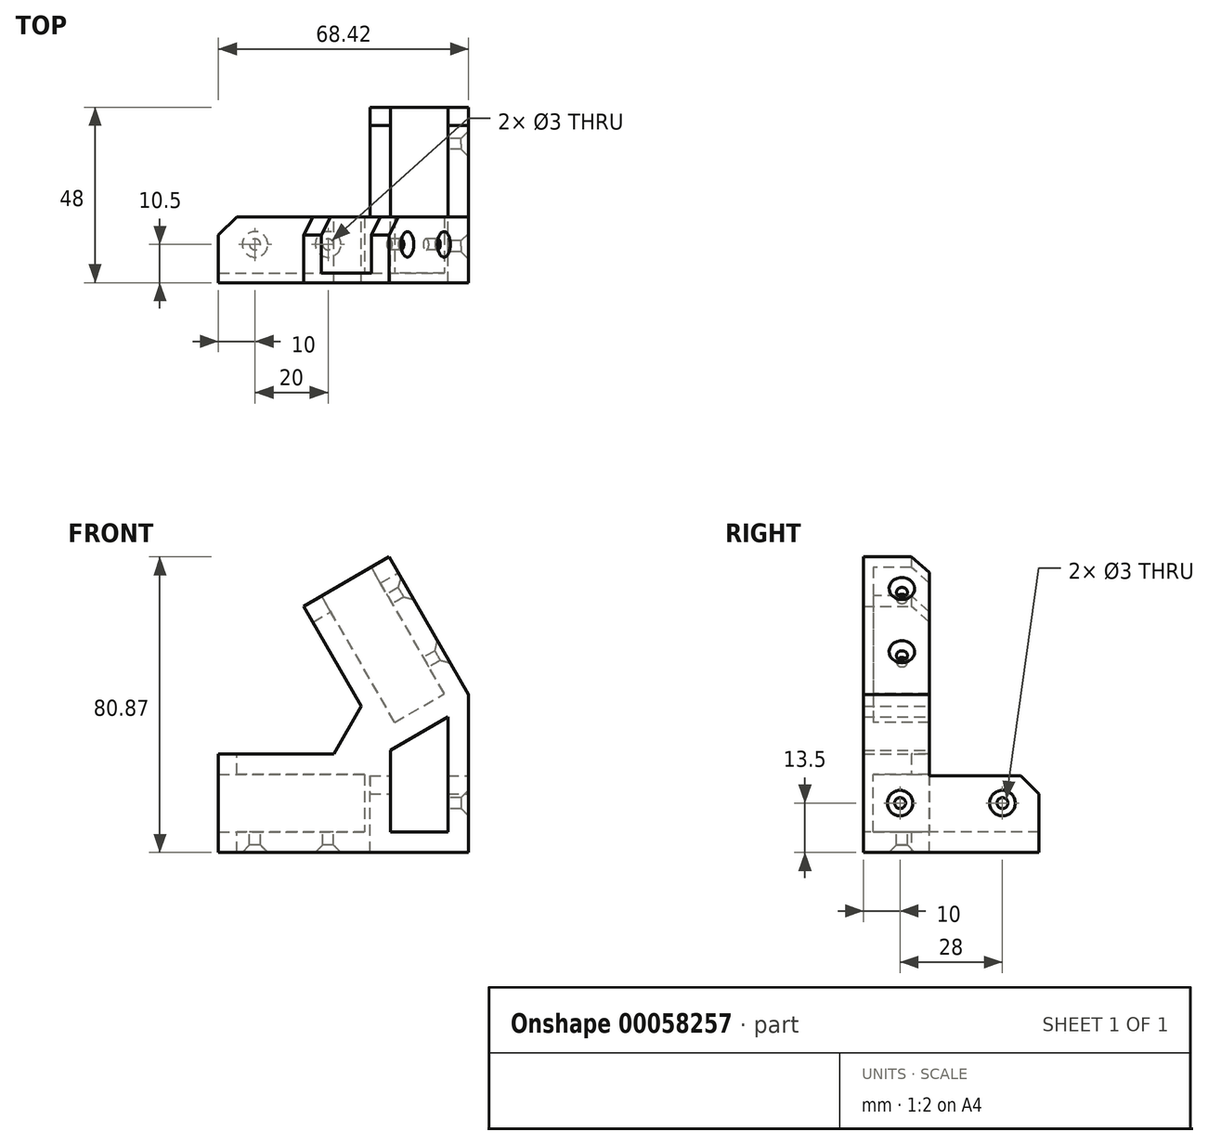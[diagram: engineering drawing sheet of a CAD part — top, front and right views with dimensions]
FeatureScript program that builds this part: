
annotation { "Feature Type Name" : "Feature", "Feature Type Description" : "" }
export const myFeature = defineFeature(function(context is Context, id is Id, definition is map)
    precondition{}
    {
        {
            var Q0;
            Q0=qCreatedBy(makeId("Front.planeOp"),FACE);
            var sketch = newSketch(context, id + "F0", { "sketchPlane" : qUnion([Q0])});
            skLineSegment(sketch, "E0", {"start": v(0, 0) * mm, "end": v(-45, 25.98) * mm, "construction": true});
            skLineSegment(sketch, "E1", {"start": v(0, 0) * mm, "end": v(-59.97, 0) * mm, "construction": true});
            skLineSegment(sketch, "E2.bottom", {"start": v(-30, 7.5) * mm, "end": v(-70, 7.5) * mm});
            skLineSegment(sketch, "E2.top", {"start": v(-30, -7.5) * mm, "end": v(-70, -7.5) * mm});
            skLineSegment(sketch, "E2.left", {"start": v(-30, 7.5) * mm, "end": v(-30, -7.5) * mm});
            skLineSegment(sketch, "E2.right", {"start": v(-70, 7.5) * mm, "end": v(-70, -7.5) * mm, "construction": true});
            skPoint(sketch, "E2.middle", {"position": v(-50, 0) * mm});
            skLineSegment(sketch, "E3", {"start": v(-70, -7.5) * mm, "end": v(-70, -13.5) * mm});
            skLineSegment(sketch, "E4", {"start": v(-70, -13.5) * mm, "end": v(-1.58, -13.5) * mm});
            skLineSegment(sketch, "E5", {"start": v(-70, 7.5) * mm, "end": v(-70, 13.5) * mm});
            skLineSegment(sketch, "E6", {"start": v(-70, 13.5) * mm, "end": v(-38.38, 13.5) * mm});
            skLineSegment(sketch, "E7.MirrorCS", {"start": v(-28.5, 64.37) * mm, "end": v(-23.3, 67.37) * mm});
            skLineSegment(sketch, "E8.MirrorCS", {"start": v(-8.5, 29.73) * mm, "end": v(-28.5, 64.37) * mm});
            skLineSegment(sketch, "E9.MirrorCS", {"start": v(-21.5, 22.23) * mm, "end": v(-8.5, 29.73) * mm});
            skLineSegment(sketch, "E10.MirrorCS", {"start": v(-21.5, 22.23) * mm, "end": v(-41.5, 56.87) * mm});
            skLineSegment(sketch, "E11.MirrorCS", {"start": v(-41.5, 56.87) * mm, "end": v(-46.7, 53.87) * mm});
            skLineSegment(sketch, "E12.MirrorCS", {"start": v(-46.7, 53.87) * mm, "end": v(-30.88, 26.5) * mm});
            skLineSegment(sketch, "E13", {"start": v(-23.3, 67.37) * mm, "end": v(-1.58, 29.73) * mm});
            skLineSegment(sketch, "E14", {"start": v(-1.58, 29.73) * mm, "end": v(-1.58, -13.5) * mm});
            skLineSegment(sketch, "E15.bottom", {"start": v(-7.58, 7.5) * mm, "end": v(-22.58, 7.5) * mm});
            skLineSegment(sketch, "E15.top", {"start": v(-7.58, -7.5) * mm, "end": v(-22.58, -7.5) * mm});
            skLineSegment(sketch, "E15.left", {"start": v(-7.58, 7.5) * mm, "end": v(-7.58, -7.5) * mm});
            skLineSegment(sketch, "E15.right", {"start": v(-22.58, 7.5) * mm, "end": v(-22.58, -7.5) * mm});
            skPoint(sketch, "E15.middle", {"position": v(-15.08, 0) * mm});
            skLineSegment(sketch, "E16", {"start": v(-30.88, 26.5) * mm, "end": v(-38.38, 13.5) * mm});
            skLineSegment(sketch, "E17", {"start": v(-30.88, 26.5) * mm, "end": v(-23.38, 13.5) * mm, "construction": true});
            skLineSegment(sketch, "E18", {"start": v(-38.38, 13.5) * mm, "end": v(-23.38, 13.5) * mm, "construction": true});
            skSolve(sketch);
        }
        {
            var Q0;
            Q0 = qSketchRegion(id + "F0", true);
            extrude(context, id + "F1", {"entities" : qUnion([Q0]), "depth" : 15 * mm});
        }
        {
            var Q0;
            Q0=makeQuery(id+"F1.opExtrude","CAP_FACE",FACE,{"disambiguationData":[OSD([sQuery(id+"F0.wireOp",EDGE,"E2.bottom"),sQuery(id+"F0.wireOp",EDGE,"E2.top"),sQuery(id+"F0.wireOp",EDGE,"E2.left"),sQuery(id+"F0.wireOp",EDGE,"E3"),sQuery(id+"F0.wireOp",EDGE,"E4"),sQuery(id+"F0.wireOp",EDGE,"E5"),sQuery(id+"F0.wireOp",EDGE,"E6"),sQuery(id+"F0.wireOp",EDGE,"E7.MirrorCS"),sQuery(id+"F0.wireOp",EDGE,"E8.MirrorCS"),sQuery(id+"F0.wireOp",EDGE,"E9.MirrorCS"),sQuery(id+"F0.wireOp",EDGE,"E10.MirrorCS"),sQuery(id+"F0.wireOp",EDGE,"E11.MirrorCS"),sQuery(id+"F0.wireOp",EDGE,"E12.MirrorCS"),sQuery(id+"F0.wireOp",EDGE,"E13"),sQuery(id+"F0.wireOp",EDGE,"E14"),sQuery(id+"F0.wireOp",EDGE,"E15.bottom"),sQuery(id+"F0.wireOp",EDGE,"E15.top"),sQuery(id+"F0.wireOp",EDGE,"E15.left"),sQuery(id+"F0.wireOp",EDGE,"E15.right")])],"isStart":false});
            var sketch = newSketch(context, id + "F2", { "sketchPlane" : qUnion([Q0])});
            skLineSegment(sketch, "E19", {"start": v(-70, 13.5) * mm, "end": v(-70, -13.5) * mm});
            skLineSegment(sketch, "E20", {"start": v(-46.7, 53.87) * mm, "end": v(-23.3, 67.37) * mm});
            skLineSegment(sketch, "E21.0", {"start": v(-23.3, 67.37) * mm, "end": v(-1.58, 29.73) * mm});
            skLineSegment(sketch, "E21.1", {"start": v(-1.58, 29.73) * mm, "end": v(-1.58, -13.5) * mm});
            skLineSegment(sketch, "E21.2", {"start": v(-70, -13.5) * mm, "end": v(-1.58, -13.5) * mm});
            skLineSegment(sketch, "E21.3", {"start": v(-70, 13.5) * mm, "end": v(-70, 13.5) * mm});
            skLineSegment(sketch, "E22.0", {"start": v(-7.58, 7.5) * mm, "end": v(-22.58, 7.5) * mm});
            skLineSegment(sketch, "E22.1", {"start": v(-22.58, 7.5) * mm, "end": v(-22.58, -7.5) * mm});
            skLineSegment(sketch, "E22.2", {"start": v(-7.58, -7.5) * mm, "end": v(-22.58, -7.5) * mm});
            skLineSegment(sketch, "E22.3", {"start": v(-7.58, 7.5) * mm, "end": v(-7.58, -7.5) * mm});
            skLineSegment(sketch, "E23.0", {"start": v(-46.7, 53.87) * mm, "end": v(-30.88, 26.5) * mm});
            skLineSegment(sketch, "E23.1", {"start": v(-70, 13.5) * mm, "end": v(-38.38, 13.5) * mm});
            skLineSegment(sketch, "E23.2", {"start": v(-30.88, 26.5) * mm, "end": v(-38.38, 13.5) * mm});
            skSolve(sketch);
        }
        {
            var Q0;
            Q0 = qSketchRegion(id + "F2", true);
            extrude(context, id + "F3", {"entities" : qUnion([Q0]), "operationType" : NewBodyOperationType.ADD, "depth" : 3 * mm});
        }
        {
            var Q0;
            Q0=makeQuery(id+"F1.opExtrude","CAP_FACE",FACE,{"disambiguationData":[OSD([sQuery(id+"F0.wireOp",EDGE,"E2.bottom"),sQuery(id+"F0.wireOp",EDGE,"E2.top"),sQuery(id+"F0.wireOp",EDGE,"E2.left"),sQuery(id+"F0.wireOp",EDGE,"E3"),sQuery(id+"F0.wireOp",EDGE,"E4"),sQuery(id+"F0.wireOp",EDGE,"E5"),sQuery(id+"F0.wireOp",EDGE,"E6"),sQuery(id+"F0.wireOp",EDGE,"E7.MirrorCS"),sQuery(id+"F0.wireOp",EDGE,"E8.MirrorCS"),sQuery(id+"F0.wireOp",EDGE,"E9.MirrorCS"),sQuery(id+"F0.wireOp",EDGE,"E10.MirrorCS"),sQuery(id+"F0.wireOp",EDGE,"E11.MirrorCS"),sQuery(id+"F0.wireOp",EDGE,"E12.MirrorCS"),sQuery(id+"F0.wireOp",EDGE,"E13"),sQuery(id+"F0.wireOp",EDGE,"E14"),sQuery(id+"F0.wireOp",EDGE,"E15.bottom"),sQuery(id+"F0.wireOp",EDGE,"E15.top"),sQuery(id+"F0.wireOp",EDGE,"E15.left"),sQuery(id+"F0.wireOp",EDGE,"E15.right")])],"isStart":true});
            var sketch = newSketch(context, id + "F4", { "sketchPlane" : qUnion([Q0])});
            skLineSegment(sketch, "E24.0", {"start": v(7.58, 7.5) * mm, "end": v(22.58, 7.5) * mm, "construction": true});
            skLineSegment(sketch, "E24.1", {"start": v(7.58, 7.5) * mm, "end": v(7.58, -7.5) * mm});
            skLineSegment(sketch, "E24.2", {"start": v(7.58, -7.5) * mm, "end": v(22.58, -7.5) * mm});
            skLineSegment(sketch, "E24.3", {"start": v(22.58, 7.5) * mm, "end": v(22.58, -7.5) * mm});
            skLineSegment(sketch, "E25", {"start": v(7.58, 7.5) * mm, "end": v(22.58, -7.5) * mm, "construction": true});
            skPoint(sketch, "E26.middle", {"position": v(15.08, 0) * mm});
            skLineSegment(sketch, "E27", {"start": v(7.58, 7.5) * mm, "end": v(1.58, 7.5) * mm});
            skLineSegment(sketch, "E28", {"start": v(1.58, 7.5) * mm, "end": v(1.58, -13.5) * mm});
            skLineSegment(sketch, "E29", {"start": v(1.58, -13.5) * mm, "end": v(28.58, -13.5) * mm});
            skLineSegment(sketch, "E30", {"start": v(28.58, -13.5) * mm, "end": v(28.58, 7.5) * mm});
            skLineSegment(sketch, "E31", {"start": v(28.58, 7.5) * mm, "end": v(22.58, 7.5) * mm});
            skSolve(sketch);
        }
        {
            var Q0;
            Q0 = qSketchRegion(id + "F4", true);
            extrude(context, id + "F5", {"entities" : qUnion([Q0]), "operationType" : NewBodyOperationType.ADD, "depth" : 30 * mm});
        }
        {
            var Q0;
            Q0=makeQuery(id+"F1.opExtrude","SWEPT_FACE",FACE,{"disambiguationData":[OSD([sQuery(id+"F0.wireOp",EDGE,"E2.top")])]});
            var sketch = newSketch(context, id + "F6", { "sketchPlane" : qUnion([Q0])});
            skLineSegment(sketch, "E32", {"start": v(-30, -7.5) * mm, "end": v(-70, -7.5) * mm, "construction": true});
            skCircle(sketch, "E33", {"center": v(-40, -7.5) * mm, "radius": 1.5 * mm});
            skCircle(sketch, "E34", {"center": v(-60, -7.5) * mm, "radius": 1.5 * mm});
            skSolve(sketch);
        }
        {
            var Q0;
            Q0 = qSketchRegion(id + "F6", true);
            extrude(context, id + "F7", {"entities" : qUnion([Q0]), "operationType" : NewBodyOperationType.REMOVE, "endBound" : BoundingType.THROUGH_ALL, "oppositeDirection" : true, "depth" : 25 * mm});
        }
        {
            var Q0;
            Q0=makeQuery(id+"F1.opExtrude","SWEPT_FACE",FACE,{"disambiguationData":[OSD([sQuery(id+"F0.wireOp",EDGE,"E8.MirrorCS")])]});
            var sketch = newSketch(context, id + "F8", { "sketchPlane" : qUnion([Q0])});
            skLineSegment(sketch, "E35", {"start": v(7.5, 30) * mm, "end": v(7.5, 70) * mm, "construction": true});
            skCircle(sketch, "E36", {"center": v(7.5, 40) * mm, "radius": 1.5 * mm});
            skCircle(sketch, "E37", {"center": v(7.5, 60) * mm, "radius": 1.5 * mm});
            skSolve(sketch);
        }
        {
            var Q0;
            Q0 = qSketchRegion(id + "F8", true);
            extrude(context, id + "F9", {"entities" : qUnion([Q0]), "operationType" : NewBodyOperationType.REMOVE, "endBound" : BoundingType.THROUGH_ALL, "oppositeDirection" : true, "depth" : 25 * mm});
        }
        {
            var Q0;
            Q0=makeQuery(id+"F5.boolean.opBoolean","MERGE",FACE,{"derivedFrom":[makeQuery(id+"F3.boolean.opBoolean","MERGE",FACE,{"derivedFrom":[makeQuery(id+"F1.opExtrude","SWEPT_FACE",FACE,{"disambiguationData":[OSD([sQuery(id+"F0.wireOp",EDGE,"E15.left")])]}),makeQuery(id+"F3.opExtrude","SWEPT_FACE",FACE,{"disambiguationData":[OSD([sQuery(id+"F2.wireOp",EDGE,"E22.3")])]})]}),makeQuery(id+"F5.opExtrude","SWEPT_FACE",FACE,{"disambiguationData":[OSD([sQuery(id+"F4.wireOp",EDGE,"E24.1")])]})]});
            var sketch = newSketch(context, id + "F10", { "sketchPlane" : qUnion([Q0])});
            skLineSegment(sketch, "E38", {"start": v(18, 0) * mm, "end": v(-30, 0) * mm, "construction": true});
            skCircle(sketch, "E39", {"center": v(-20, 0) * mm, "radius": 1.5 * mm});
            skCircle(sketch, "E40", {"center": v(8, 0) * mm, "radius": 1.5 * mm});
            skSolve(sketch);
        }
        {
            var Q0;
            Q0 = qSketchRegion(id + "F10", true);
            extrude(context, id + "F11", {"entities" : qUnion([Q0]), "operationType" : NewBodyOperationType.REMOVE, "endBound" : BoundingType.THROUGH_ALL, "oppositeDirection" : true, "depth" : 25 * mm});
        }
        {
            var Q0;
            Q0=makeQuery(id+"F1.opExtrude","CAP_EDGE",EDGE,{"disambiguationData":[OSD([sQuery(id+"F0.wireOp",EDGE,"E7.MirrorCS")])],"isStart":true});
            var Q1;
            Q1=makeQuery(id+"F1.opExtrude","CAP_EDGE",EDGE,{"disambiguationData":[OSD([sQuery(id+"F0.wireOp",EDGE,"E11.MirrorCS")])],"isStart":true});
            var Q2;
            Q2=makeQuery(id+"F5.opExtrude","CAP_EDGE",EDGE,{"disambiguationData":[OSD([sQuery(id+"F4.wireOp",EDGE,"E27")])],"isStart":false});
            var Q3;
            Q3=makeQuery(id+"F5.opExtrude","CAP_EDGE",EDGE,{"disambiguationData":[OSD([sQuery(id+"F4.wireOp",EDGE,"E31")])],"isStart":false});
            var Q4;
            Q4=makeQuery(id+"F1.opExtrude","CAP_EDGE",EDGE,{"disambiguationData":[OSD([sQuery(id+"F0.wireOp",EDGE,"E5")])],"isStart":true});
            var Q5;
            Q5=makeQuery(id+"F1.opExtrude","CAP_EDGE",EDGE,{"disambiguationData":[OSD([sQuery(id+"F0.wireOp",EDGE,"E3")])],"isStart":true});
            chamfer(context, id + "F12", {"entities" : qUnion([Q0, Q1, Q2, Q3, Q4, Q5]), "width" : 5 * mm, "tangentPropagation" : true});
        }
        {
            var Q0;
            Q0=makeQuery(id+"F11.boolean.opBoolean","INTERSECT",EDGE,{"derivedFrom":[makeQuery(id+"F5.boolean.opBoolean","MERGE",FACE,{"derivedFrom":[makeQuery(id+"F3.boolean.opBoolean","MERGE",FACE,{"derivedFrom":[makeQuery(id+"F1.opExtrude","SWEPT_FACE",FACE,{"disambiguationData":[OSD([sQuery(id+"F0.wireOp",EDGE,"E14")])]}),makeQuery(id+"F3.opExtrude","SWEPT_FACE",FACE,{"disambiguationData":[OSD([sQuery(id+"F2.wireOp",EDGE,"E21.1")])]})]}),makeQuery(id+"F5.opExtrude","SWEPT_FACE",FACE,{"disambiguationData":[OSD([sQuery(id+"F4.wireOp",EDGE,"E28")])]})]}),makeQuery(id+"F11.opExtrude","SWEPT_FACE",FACE,{"disambiguationData":[OSD([sQuery(id+"F10.wireOp",EDGE,"E40")])]})]});
            var Q1;
            Q1=makeQuery(id+"F11.boolean.opBoolean","INTERSECT",EDGE,{"derivedFrom":[makeQuery(id+"F5.boolean.opBoolean","MERGE",FACE,{"derivedFrom":[makeQuery(id+"F3.boolean.opBoolean","MERGE",FACE,{"derivedFrom":[makeQuery(id+"F1.opExtrude","SWEPT_FACE",FACE,{"disambiguationData":[OSD([sQuery(id+"F0.wireOp",EDGE,"E14")])]}),makeQuery(id+"F3.opExtrude","SWEPT_FACE",FACE,{"disambiguationData":[OSD([sQuery(id+"F2.wireOp",EDGE,"E21.1")])]})]}),makeQuery(id+"F5.opExtrude","SWEPT_FACE",FACE,{"disambiguationData":[OSD([sQuery(id+"F4.wireOp",EDGE,"E28")])]})]}),makeQuery(id+"F11.opExtrude","SWEPT_FACE",FACE,{"disambiguationData":[OSD([sQuery(id+"F10.wireOp",EDGE,"E39")])]})]});
            var Q2;
            Q2=makeQuery(id+"F9.boolean.opBoolean","INTERSECT",EDGE,{"derivedFrom":[makeQuery(id+"F3.boolean.opBoolean","MERGE",FACE,{"derivedFrom":[makeQuery(id+"F1.opExtrude","SWEPT_FACE",FACE,{"disambiguationData":[OSD([sQuery(id+"F0.wireOp",EDGE,"E13")])]}),makeQuery(id+"F3.opExtrude","SWEPT_FACE",FACE,{"disambiguationData":[OSD([sQuery(id+"F2.wireOp",EDGE,"E21.0")])]})]}),makeQuery(id+"F9.opExtrude","SWEPT_FACE",FACE,{"disambiguationData":[OSD([sQuery(id+"F8.wireOp",EDGE,"E36")])]})]});
            var Q3;
            Q3=makeQuery(id+"F9.boolean.opBoolean","INTERSECT",EDGE,{"derivedFrom":[makeQuery(id+"F3.boolean.opBoolean","MERGE",FACE,{"derivedFrom":[makeQuery(id+"F1.opExtrude","SWEPT_FACE",FACE,{"disambiguationData":[OSD([sQuery(id+"F0.wireOp",EDGE,"E13")])]}),makeQuery(id+"F3.opExtrude","SWEPT_FACE",FACE,{"disambiguationData":[OSD([sQuery(id+"F2.wireOp",EDGE,"E21.0")])]})]}),makeQuery(id+"F9.opExtrude","SWEPT_FACE",FACE,{"disambiguationData":[OSD([sQuery(id+"F8.wireOp",EDGE,"E37")])]})]});
            var Q4;
            Q4=makeQuery(id+"F7.boolean.opBoolean","INTERSECT",EDGE,{"derivedFrom":[makeQuery(id+"F5.boolean.opBoolean","MERGE",FACE,{"derivedFrom":[makeQuery(id+"F3.boolean.opBoolean","MERGE",FACE,{"derivedFrom":[makeQuery(id+"F1.opExtrude","SWEPT_FACE",FACE,{"disambiguationData":[OSD([sQuery(id+"F0.wireOp",EDGE,"E4")])]}),makeQuery(id+"F3.opExtrude","SWEPT_FACE",FACE,{"disambiguationData":[OSD([sQuery(id+"F2.wireOp",EDGE,"E21.2")])]})]}),makeQuery(id+"F5.opExtrude","SWEPT_FACE",FACE,{"disambiguationData":[OSD([sQuery(id+"F4.wireOp",EDGE,"E29")])]})]}),makeQuery(id+"F7.opExtrude","SWEPT_FACE",FACE,{"disambiguationData":[OSD([sQuery(id+"F6.wireOp",EDGE,"E33")])]})]});
            var Q5;
            Q5=makeQuery(id+"F7.boolean.opBoolean","INTERSECT",EDGE,{"derivedFrom":[makeQuery(id+"F5.boolean.opBoolean","MERGE",FACE,{"derivedFrom":[makeQuery(id+"F3.boolean.opBoolean","MERGE",FACE,{"derivedFrom":[makeQuery(id+"F1.opExtrude","SWEPT_FACE",FACE,{"disambiguationData":[OSD([sQuery(id+"F0.wireOp",EDGE,"E4")])]}),makeQuery(id+"F3.opExtrude","SWEPT_FACE",FACE,{"disambiguationData":[OSD([sQuery(id+"F2.wireOp",EDGE,"E21.2")])]})]}),makeQuery(id+"F5.opExtrude","SWEPT_FACE",FACE,{"disambiguationData":[OSD([sQuery(id+"F4.wireOp",EDGE,"E29")])]})]}),makeQuery(id+"F7.opExtrude","SWEPT_FACE",FACE,{"disambiguationData":[OSD([sQuery(id+"F6.wireOp",EDGE,"E34")])]})]});
            chamfer(context, id + "F13", {"entities" : qUnion([Q0, Q1, Q2, Q3, Q4, Q5]), "width" : 2 * mm, "tangentPropagation" : true});
        }
        {
            var Q0;
            Q0=makeQuery(id+"F3.opExtrude","CAP_FACE",FACE,{"disambiguationData":[OSD([sQuery(id+"F2.wireOp",EDGE,"E19"),sQuery(id+"F2.wireOp",EDGE,"E20"),sQuery(id+"F2.wireOp",EDGE,"E21.0"),sQuery(id+"F2.wireOp",EDGE,"E21.1"),sQuery(id+"F2.wireOp",EDGE,"E21.2"),sQuery(id+"F2.wireOp",EDGE,"E22.0"),sQuery(id+"F2.wireOp",EDGE,"E22.1"),sQuery(id+"F2.wireOp",EDGE,"E22.2"),sQuery(id+"F2.wireOp",EDGE,"E22.3"),sQuery(id+"F2.wireOp",EDGE,"E23.0"),sQuery(id+"F2.wireOp",EDGE,"E23.1"),sQuery(id+"F2.wireOp",EDGE,"E23.2")])],"isStart":false});
            var sketch = newSketch(context, id + "F14", { "sketchPlane" : qUnion([Q0])});
            skLineSegment(sketch, "E41", {"start": v(-22.58, 7.5) * mm, "end": v(-7.58, -7.5) * mm, "construction": true});
            skLineSegment(sketch, "E42.bottom", {"start": v(-7.23, 7.85) * mm, "end": v(-22.93, 7.85) * mm});
            skLineSegment(sketch, "E42.top", {"start": v(-7.23, -7.85) * mm, "end": v(-22.93, -7.85) * mm});
            skLineSegment(sketch, "E42.left", {"start": v(-7.23, 7.85) * mm, "end": v(-7.23, -7.85) * mm});
            skLineSegment(sketch, "E42.right", {"start": v(-22.93, 7.85) * mm, "end": v(-22.93, -7.85) * mm});
            skPoint(sketch, "E42.middle", {"position": v(-15.08, 0) * mm});
            skSolve(sketch);
        }
        {
            var Q0;
            Q0 = qSketchRegion(id + "F14", true);
            extrude(context, id + "F15", {"entities" : qUnion([Q0]), "operationType" : NewBodyOperationType.REMOVE, "endBound" : BoundingType.THROUGH_ALL, "oppositeDirection" : true, "depth" : 25 * mm});
        }
        {
            var Q0;
            Q0=makeQuery(id+"F1.opExtrude","SWEPT_FACE",FACE,{"disambiguationData":[OSD([sQuery(id+"F0.wireOp",EDGE,"E9.MirrorCS")])]});
            var sketch = newSketch(context, id + "F16", { "sketchPlane" : qUnion([Q0])});
            skLineSegment(sketch, "E43", {"start": v(-7.5, 0) * mm, "end": v(7.5, -15) * mm, "construction": true});
            skLineSegment(sketch, "E44.bottom", {"start": v(7.85, 0.35) * mm, "end": v(-7.85, 0.35) * mm});
            skLineSegment(sketch, "E44.top", {"start": v(7.85, -15.35) * mm, "end": v(-7.85, -15.35) * mm});
            skLineSegment(sketch, "E44.left", {"start": v(7.85, 0.35) * mm, "end": v(7.85, -15.35) * mm});
            skLineSegment(sketch, "E44.right", {"start": v(-7.85, 0.35) * mm, "end": v(-7.85, -15.35) * mm});
            skPoint(sketch, "E44.middle", {"position": v(0, -7.5) * mm});
            skSolve(sketch);
        }
        {
            var Q0;
            Q0 = qSketchRegion(id + "F16", true);
            extrude(context, id + "F17", {"entities" : qUnion([Q0]), "operationType" : NewBodyOperationType.REMOVE, "endBound" : BoundingType.THROUGH_ALL, "depth" : 25 * mm});
        }
        {
            var Q0;
            Q0=makeQuery(id+"F1.opExtrude","SWEPT_FACE",FACE,{"disambiguationData":[OSD([sQuery(id+"F0.wireOp",EDGE,"E2.left")])]});
            var sketch = newSketch(context, id + "F18", { "sketchPlane" : qUnion([Q0])});
            skLineSegment(sketch, "E45", {"start": v(0, -7.5) * mm, "end": v(15, 7.5) * mm, "construction": true});
            skLineSegment(sketch, "E46.bottom", {"start": v(-0.35, 7.85) * mm, "end": v(15.35, 7.85) * mm});
            skLineSegment(sketch, "E46.top", {"start": v(-0.35, -7.85) * mm, "end": v(15.35, -7.85) * mm});
            skLineSegment(sketch, "E46.left", {"start": v(-0.35, 7.85) * mm, "end": v(-0.35, -7.85) * mm});
            skLineSegment(sketch, "E46.right", {"start": v(15.35, 7.85) * mm, "end": v(15.35, -7.85) * mm});
            skPoint(sketch, "E46.middle", {"position": v(7.5, 0) * mm});
            skSolve(sketch);
        }
        {
            var Q0;
            Q0 = qSketchRegion(id + "F18", true);
            extrude(context, id + "F19", {"entities" : qUnion([Q0]), "operationType" : NewBodyOperationType.REMOVE, "endBound" : BoundingType.THROUGH_ALL, "depth" : 25 * mm});
        }
        {
            var Q0;
            Q0=makeQuery(id+"F1.opExtrude","CAP_FACE",FACE,{"disambiguationData":[OSD([sQuery(id+"F0.wireOp",EDGE,"E2.bottom"),sQuery(id+"F0.wireOp",EDGE,"E2.top"),sQuery(id+"F0.wireOp",EDGE,"E2.left"),sQuery(id+"F0.wireOp",EDGE,"E3"),sQuery(id+"F0.wireOp",EDGE,"E4"),sQuery(id+"F0.wireOp",EDGE,"E5"),sQuery(id+"F0.wireOp",EDGE,"E6"),sQuery(id+"F0.wireOp",EDGE,"E7.MirrorCS"),sQuery(id+"F0.wireOp",EDGE,"E8.MirrorCS"),sQuery(id+"F0.wireOp",EDGE,"E9.MirrorCS"),sQuery(id+"F0.wireOp",EDGE,"E10.MirrorCS"),sQuery(id+"F0.wireOp",EDGE,"E11.MirrorCS"),sQuery(id+"F0.wireOp",EDGE,"E12.MirrorCS"),sQuery(id+"F0.wireOp",EDGE,"E13"),sQuery(id+"F0.wireOp",EDGE,"E14"),sQuery(id+"F0.wireOp",EDGE,"E15.bottom"),sQuery(id+"F0.wireOp",EDGE,"E15.top"),sQuery(id+"F0.wireOp",EDGE,"E15.left"),sQuery(id+"F0.wireOp",EDGE,"E15.right"),sQuery(id+"F0.wireOp",EDGE,"E16")])],"isStart":true});
            var sketch = newSketch(context, id + "F20", { "sketchPlane" : qUnion([Q0])});
            skLineSegment(sketch, "E47.0", {"start": v(7.23, 7.85) * mm, "end": v(22.93, 7.85) * mm});
            skLineSegment(sketch, "E48", {"start": v(22.93, 7.85) * mm, "end": v(22.93, 14.48) * mm});
            skLineSegment(sketch, "E49", {"start": v(22.93, 14.48) * mm, "end": v(7.23, 23.54) * mm});
            skLineSegment(sketch, "E50", {"start": v(7.23, 23.54) * mm, "end": v(7.23, 7.85) * mm});
            skSolve(sketch);
        }
        {
            var Q0;
            Q0 = qSketchRegion(id + "F20", true);
            extrude(context, id + "F21", {"entities" : qUnion([Q0]), "operationType" : NewBodyOperationType.REMOVE, "endBound" : BoundingType.THROUGH_ALL, "oppositeDirection" : true, "depth" : 25 * mm});
        }
    });
